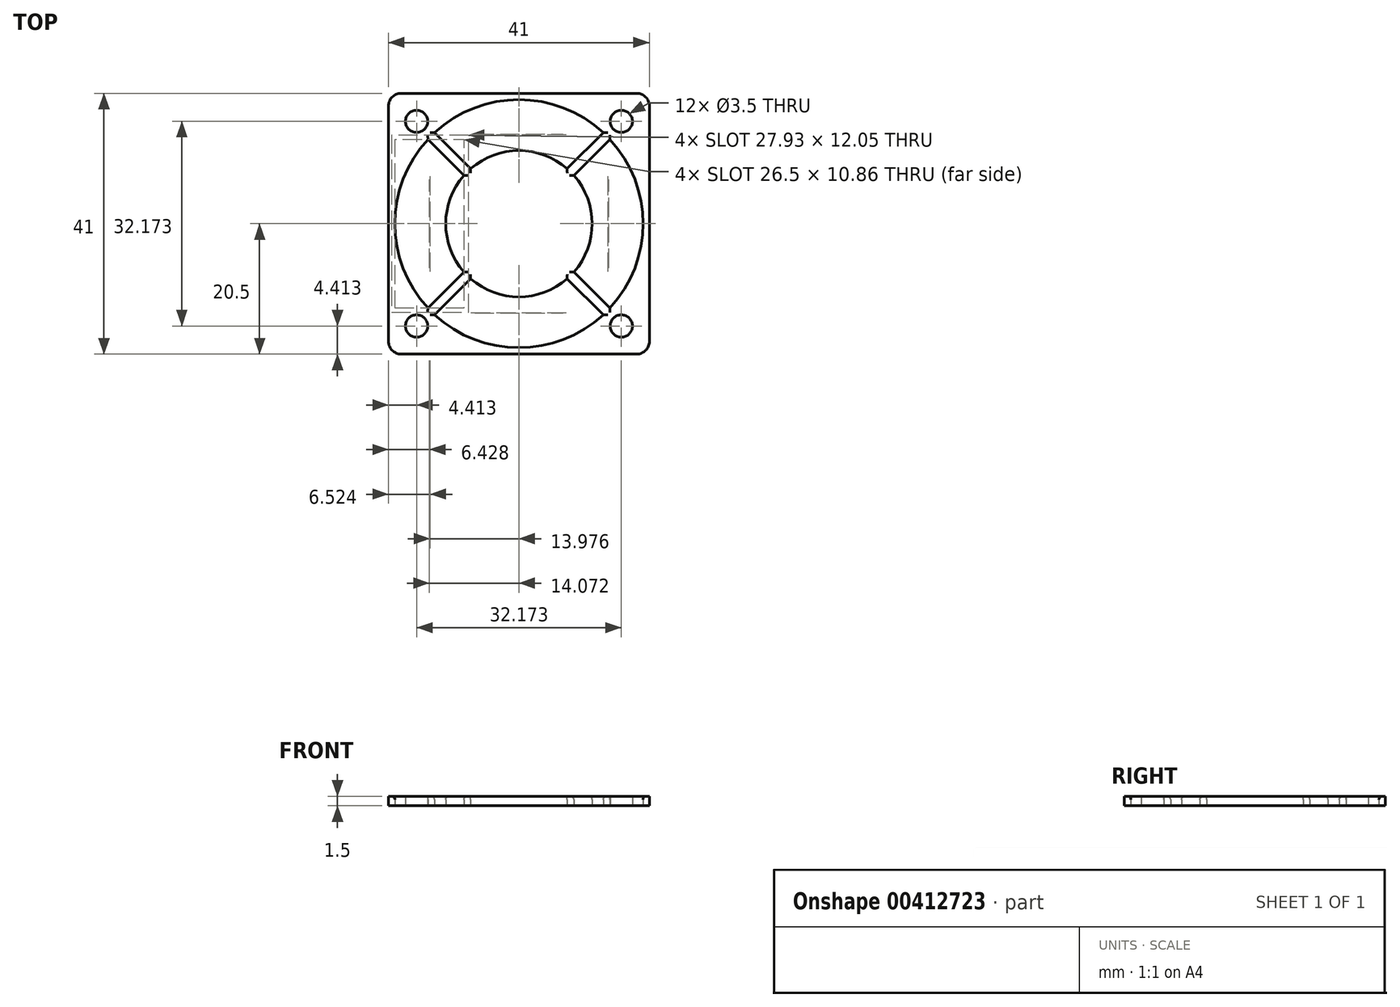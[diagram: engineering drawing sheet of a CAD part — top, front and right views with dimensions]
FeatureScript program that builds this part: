
annotation { "Feature Type Name" : "Feature", "Feature Type Description" : "" }
export const myFeature = defineFeature(function(context is Context, id is Id, definition is map)
    precondition{}
    {
        {
            var Q0;
            Q0=qCreatedBy(makeId("Top.planeOp"),FACE);
            var sketch = newSketch(context, id + "F0", { "sketchPlane" : qUnion([Q0])});
            skLineSegment(sketch, "E0.bottom", {"start": v(0, 0) * mm, "end": v(41, 0) * mm});
            skLineSegment(sketch, "E0.top", {"start": v(0, 41) * mm, "end": v(41, 41) * mm});
            skLineSegment(sketch, "E0.left", {"start": v(0, 0) * mm, "end": v(0, 41) * mm});
            skLineSegment(sketch, "E0.right", {"start": v(41, 0) * mm, "end": v(41, 41) * mm});
            skLineSegment(sketch, "E1", {"start": v(0, 0) * mm, "end": v(41, 41) * mm, "construction": true});
            skLineSegment(sketch, "E2", {"start": v(0, 41) * mm, "end": v(41, 0) * mm, "construction": true});
            skCircle(sketch, "E3", {"center": v(20.5, 20.5) * mm, "radius": 19.5 * mm});
            skCircle(sketch, "E4", {"center": v(36.59, 36.59) * mm, "radius": 1.75 * mm});
            skCircle(sketch, "E5", {"center": v(4.41, 36.59) * mm, "radius": 1.75 * mm});
            skCircle(sketch, "E6", {"center": v(4.41, 4.41) * mm, "radius": 1.75 * mm});
            skCircle(sketch, "E7", {"center": v(36.59, 4.41) * mm, "radius": 1.75 * mm});
            skLineSegment(sketch, "E8", {"start": v(4.41, 36.59) * mm, "end": v(54.9, 36.59) * mm, "construction": true});
            skLineSegment(sketch, "E9", {"start": v(4.41, 4.41) * mm, "end": v(54.03, 4.41) * mm, "construction": true});
            skLineSegment(sketch, "E10", {"start": v(4.41, 36.59) * mm, "end": v(4.41, -11.07) * mm, "construction": true});
            skCircle(sketch, "E11", {"center": v(20.5, 20.5) * mm, "radius": 11.5 * mm});
            skLineSegment(sketch, "E12", {"start": v(7.25, 34.8) * mm, "end": v(12.92, 29.14) * mm});
            skLineSegment(sketch, "E13", {"start": v(6.2, 33.75) * mm, "end": v(11.86, 28.08) * mm});
            skLineSegment(sketch, "E14", {"start": v(28.08, 29.14) * mm, "end": v(33.75, 34.8) * mm});
            skLineSegment(sketch, "E15", {"start": v(29.14, 28.08) * mm, "end": v(34.8, 33.75) * mm});
            skLineSegment(sketch, "E16", {"start": v(29.14, 12.92) * mm, "end": v(34.8, 7.25) * mm});
            skLineSegment(sketch, "E17", {"start": v(28.08, 11.86) * mm, "end": v(33.75, 6.2) * mm});
            skLineSegment(sketch, "E18", {"start": v(11.86, 12.92) * mm, "end": v(6.2, 7.25) * mm});
            skLineSegment(sketch, "E19", {"start": v(12.92, 11.86) * mm, "end": v(7.25, 6.2) * mm});
            skSolve(sketch);
        }
        {
            var Q0;
            Q0=makeQuery(id+"F0.imprint","IMPRINT",FACE,{"disambiguationData":[TD([[makeQuery(id+"F0.imprint","IMPRINT",EDGE,{"derivedFrom":sQuery(id+"F0.wireOp",EDGE,"E0.bottom")}),1.0]])]});
            var Q1;
            {var subQ0=sQuery(id+"F0.wireOp",EDGE,"E12");Q1=makeQuery(id+"F0.imprint","IMPRINT",FACE,{"disambiguationData":[TD([[makeQuery(id+"F0.imprint","IMPRINT",EDGE,{"derivedFrom":subQ0}),-1.0]])]});}
            var Q2;
            {var subQ0=sQuery(id+"F0.wireOp",EDGE,"E14");Q2=makeQuery(id+"F0.imprint","IMPRINT",FACE,{"disambiguationData":[TD([[makeQuery(id+"F0.imprint","IMPRINT",EDGE,{"derivedFrom":subQ0}),-1.0]])]});}
            var Q3;
            {var subQ0=sQuery(id+"F0.wireOp",EDGE,"E16");Q3=makeQuery(id+"F0.imprint","IMPRINT",FACE,{"disambiguationData":[TD([[makeQuery(id+"F0.imprint","IMPRINT",EDGE,{"derivedFrom":subQ0}),-1.0]])]});}
            var Q4;
            {var subQ0=sQuery(id+"F0.wireOp",EDGE,"E18");Q4=makeQuery(id+"F0.imprint","IMPRINT",FACE,{"disambiguationData":[TD([[makeQuery(id+"F0.imprint","IMPRINT",EDGE,{"derivedFrom":subQ0}),1.0]])]});}
            var Q5;
            {var subQ0=sQuery(id+"F0.wireOp",EDGE,"E11");var subQ4=makeQuery(id+"F0.imprint","INTERSECT",VERTEX,{"derivedFrom":[subQ0,sQuery(id+"F0.wireOp",EDGE,"E14")]});Q5=makeQuery(id+"F0.imprint","IMPRINT",FACE,{"disambiguationData":[TD([[makeQuery(id+"F0.imprint","IMPRINT",EDGE,{"disambiguationData":[TD([[subQ4,1.0]])],"derivedFrom":subQ0}),1.0]])]});}
            extrude(context, id + "F1", {"entities" : qUnion([Q0, Q1, Q2, Q3, Q4, Q5]), "depth" : 1.5 * mm});
        }
        {
            var Q0;
            Q0=makeQuery(id+"F1.opExtrude","CAP_EDGE",EDGE,{"disambiguationData":[OSD([sQuery(id+"F0.wireOp",EDGE,"E12")])],"isStart":false});
            var Q1;
            {var subQ0=sQuery(id+"F0.wireOp",EDGE,"E11");Q1=makeQuery(id+"F1.opExtrude","CAP_EDGE",EDGE,{"disambiguationData":[OSD([subQ0]),TDD([makeQuery(id+"F0.imprint","IMPRINT",EDGE,{"disambiguationData":[TD([[makeQuery(id+"F0.imprint","INTERSECT",VERTEX,{"derivedFrom":[subQ0,sQuery(id+"F0.wireOp",EDGE,"E12")]}),1.0]])],"derivedFrom":subQ0})])],"isStart":false});}
            var Q2;
            {var subQ0=sQuery(id+"F0.wireOp",EDGE,"E3");Q2=makeQuery(id+"F1.opExtrude","CAP_EDGE",EDGE,{"disambiguationData":[OSD([subQ0]),TDD([makeQuery(id+"F0.imprint","IMPRINT",EDGE,{"disambiguationData":[TD([[makeQuery(id+"F0.imprint","INTERSECT",VERTEX,{"derivedFrom":[subQ0,sQuery(id+"F0.wireOp",EDGE,"E13")]}),-1.0]])],"derivedFrom":subQ0})])],"isStart":false});}
            var Q3;
            {var subQ0=sQuery(id+"F0.wireOp",EDGE,"E3");Q3=makeQuery(id+"F1.opExtrude","CAP_EDGE",EDGE,{"disambiguationData":[OSD([subQ0]),TDD([makeQuery(id+"F0.imprint","IMPRINT",EDGE,{"disambiguationData":[TD([[makeQuery(id+"F0.imprint","INTERSECT",VERTEX,{"derivedFrom":[subQ0,sQuery(id+"F0.wireOp",EDGE,"E17")]}),1.0]])],"derivedFrom":subQ0})])],"isStart":false});}
            var Q4;
            Q4=makeQuery(id+"F1.opExtrude","CAP_EDGE",EDGE,{"disambiguationData":[OSD([sQuery(id+"F0.wireOp",EDGE,"E18")])],"isStart":false});
            var Q5;
            Q5=makeQuery(id+"F1.opExtrude","CAP_EDGE",EDGE,{"disambiguationData":[OSD([sQuery(id+"F0.wireOp",EDGE,"E16")])],"isStart":false});
            var Q6;
            Q6=makeQuery(id+"F1.opExtrude","CAP_EDGE",EDGE,{"disambiguationData":[OSD([sQuery(id+"F0.wireOp",EDGE,"E13")])],"isStart":false});
            var Q7;
            Q7=makeQuery(id+"F1.opExtrude","CAP_EDGE",EDGE,{"disambiguationData":[OSD([sQuery(id+"F0.wireOp",EDGE,"E19")])],"isStart":false});
            var Q8;
            {var subQ0=sQuery(id+"F0.wireOp",EDGE,"E11");Q8=makeQuery(id+"F1.opExtrude","CAP_EDGE",EDGE,{"disambiguationData":[OSD([subQ0]),TDD([makeQuery(id+"F0.imprint","IMPRINT",EDGE,{"disambiguationData":[TD([[makeQuery(id+"F0.imprint","INTERSECT",VERTEX,{"derivedFrom":[subQ0,sQuery(id+"F0.wireOp",EDGE,"E17")]}),1.0]])],"derivedFrom":subQ0})])],"isStart":false});}
            var Q9;
            {var subQ0=sQuery(id+"F0.wireOp",EDGE,"E11");Q9=makeQuery(id+"F1.opExtrude","CAP_EDGE",EDGE,{"disambiguationData":[OSD([subQ0]),TDD([makeQuery(id+"F0.imprint","IMPRINT",EDGE,{"disambiguationData":[TD([[makeQuery(id+"F0.imprint","INTERSECT",VERTEX,{"derivedFrom":[subQ0,sQuery(id+"F0.wireOp",EDGE,"E13")]}),-1.0]])],"derivedFrom":subQ0})])],"isStart":false});}
            var Q10;
            {var subQ0=sQuery(id+"F0.wireOp",EDGE,"E11");Q10=makeQuery(id+"F1.opExtrude","CAP_EDGE",EDGE,{"disambiguationData":[OSD([subQ0]),TDD([makeQuery(id+"F0.imprint","IMPRINT",EDGE,{"disambiguationData":[TD([[makeQuery(id+"F0.imprint","INTERSECT",VERTEX,{"derivedFrom":[subQ0,sQuery(id+"F0.wireOp",EDGE,"E15")]}),1.0]])],"derivedFrom":subQ0})])],"isStart":false});}
            var Q11;
            Q11=makeQuery(id+"F1.opExtrude","CAP_EDGE",EDGE,{"disambiguationData":[OSD([sQuery(id+"F0.wireOp",EDGE,"E17")])],"isStart":false});
            var Q12;
            {var subQ0=sQuery(id+"F0.wireOp",EDGE,"E3");Q12=makeQuery(id+"F1.opExtrude","CAP_EDGE",EDGE,{"disambiguationData":[OSD([subQ0]),TDD([makeQuery(id+"F0.imprint","IMPRINT",EDGE,{"disambiguationData":[TD([[makeQuery(id+"F0.imprint","INTERSECT",VERTEX,{"derivedFrom":[subQ0,sQuery(id+"F0.wireOp",EDGE,"E15")]}),1.0]])],"derivedFrom":subQ0})])],"isStart":false});}
            var Q13;
            Q13=makeQuery(id+"F1.opExtrude","CAP_EDGE",EDGE,{"disambiguationData":[OSD([sQuery(id+"F0.wireOp",EDGE,"E15")])],"isStart":false});
            var Q14;
            Q14=makeQuery(id+"F1.opExtrude","CAP_EDGE",EDGE,{"disambiguationData":[OSD([sQuery(id+"F0.wireOp",EDGE,"E14")])],"isStart":false});
            var Q15;
            {var subQ0=sQuery(id+"F0.wireOp",EDGE,"E3");Q15=makeQuery(id+"F1.opExtrude","CAP_EDGE",EDGE,{"disambiguationData":[OSD([subQ0]),TDD([makeQuery(id+"F0.imprint","IMPRINT",EDGE,{"disambiguationData":[TD([[makeQuery(id+"F0.imprint","INTERSECT",VERTEX,{"derivedFrom":[subQ0,sQuery(id+"F0.wireOp",EDGE,"E12")]}),1.0]])],"derivedFrom":subQ0})])],"isStart":false});}
            fillet(context, id + "F2", {"entities" : qUnion([Q0, Q1, Q2, Q3, Q4, Q5, Q6, Q7, Q8, Q9, Q10, Q11, Q12, Q13, Q14, Q15]), "radius" : 0.5 * mm, "tangentPropagation" : true, "allowEdgeOverflow" : false});
        }
        {
            var Q0;
            Q0=makeQuery(id+"F1.opExtrude","SWEPT_EDGE",EDGE,{"disambiguationData":[OSD([sQuery(id+"F0.wireOp",EDGE,"E0.top"),sQuery(id+"F0.wireOp",EDGE,"E0.left")])]});
            var Q1;
            Q1=makeQuery(id+"F1.opExtrude","SWEPT_EDGE",EDGE,{"disambiguationData":[OSD([sQuery(id+"F0.wireOp",EDGE,"E0.bottom"),sQuery(id+"F0.wireOp",EDGE,"E0.left")])]});
            var Q2;
            Q2=makeQuery(id+"F1.opExtrude","SWEPT_EDGE",EDGE,{"disambiguationData":[OSD([sQuery(id+"F0.wireOp",EDGE,"E0.top"),sQuery(id+"F0.wireOp",EDGE,"E0.right")])]});
            var Q3;
            Q3=makeQuery(id+"F1.opExtrude","SWEPT_EDGE",EDGE,{"disambiguationData":[OSD([sQuery(id+"F0.wireOp",EDGE,"E0.bottom"),sQuery(id+"F0.wireOp",EDGE,"E0.right")])]});
            fillet(context, id + "F3", {"entities" : qUnion([Q0, Q1, Q2, Q3]), "radius" : 2 * mm, "tangentPropagation" : true, "allowEdgeOverflow" : false});
        }
    });
